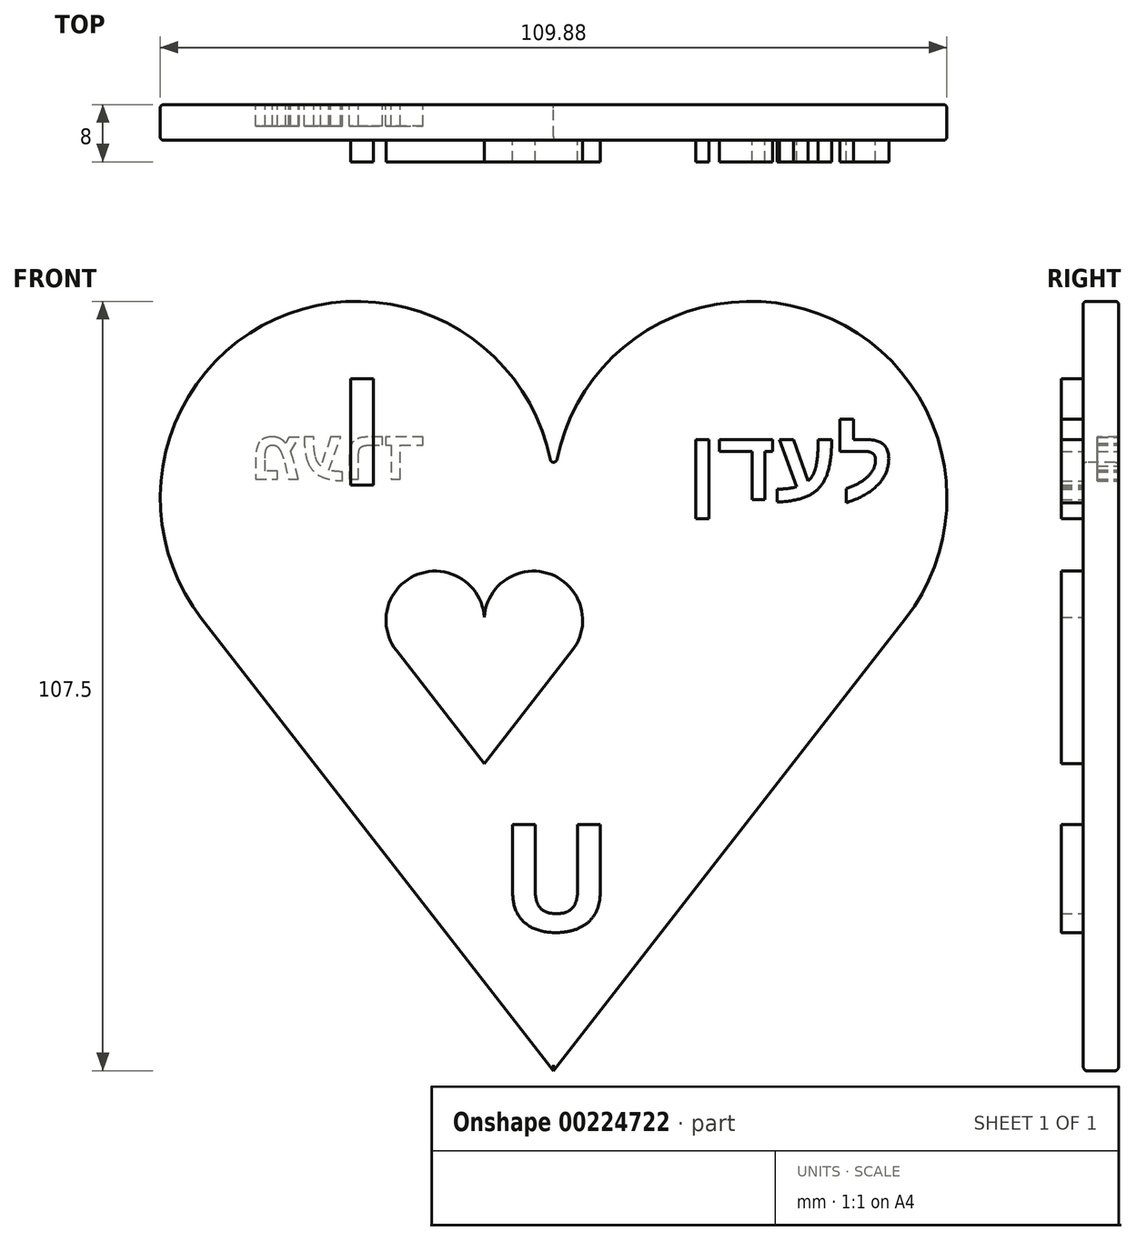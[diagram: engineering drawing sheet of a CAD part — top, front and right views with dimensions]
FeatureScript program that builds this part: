
annotation { "Feature Type Name" : "Feature", "Feature Type Description" : "" }
export const myFeature = defineFeature(function(context is Context, id is Id, definition is map)
    precondition{}
    {
        {
            var Q0;
            Q0=qCreatedBy(makeId("Front.planeOp"),FACE);
            var sketch = newSketch(context, id + "F0", { "sketchPlane" : qUnion([Q0])});
            skArc(sketch, "E0", {"start": v(49.14, 10.3) * mm, "mid": v(37.13, 52.91) * mm, "end": v(0, 28.79) * mm});
            skLineSegment(sketch, "E1", {"start": v(0, 28.79) * mm, "end": v(0, -52.83) * mm});
            skLineSegment(sketch, "E2", {"start": v(0, -52.83) * mm, "end": v(49.14, 10.3) * mm});
            skArc(sketch, "E3.MirrorCS", {"start": v(-49.14, 10.3) * mm, "mid": v(-37.13, 52.91) * mm, "end": v(0, 28.79) * mm});
            skLineSegment(sketch, "E4.MirrorCS", {"start": v(0, -52.83) * mm, "end": v(-49.14, 10.3) * mm});
            skSolve(sketch);
        }
        {
            var Q0;
            Q0=makeQuery(id+"F0.imprint","IMPRINT",FACE,{"disambiguationData":[TD([[makeQuery(id+"F0.imprint","IMPRINT",EDGE,{"derivedFrom":sQuery(id+"F0.wireOp",EDGE,"E1")}),-1.0]])]});
            var Q1;
            Q1=makeQuery(id+"F0.imprint","IMPRINT",FACE,{"disambiguationData":[TD([[makeQuery(id+"F0.imprint","IMPRINT",EDGE,{"derivedFrom":sQuery(id+"F0.wireOp",EDGE,"E0")}),1.0]])]});
            extrude(context, id + "F1", {"entities" : qUnion([Q0, Q1]), "depth" : 5 * mm});
        }
        {
            var Q0;
            Q0=qCreatedBy(makeId("Front.planeOp"),FACE);
            var sketch = newSketch(context, id + "F2", { "sketchPlane" : qUnion([Q0])});
            skArc(sketch, "E5", {"start": v(2.61, 5.88) * mm, "mid": v(-0.4, 16.54) * mm, "end": v(-9.67, 10.5) * mm});
            skLineSegment(sketch, "E6", {"start": v(-9.67, 10.5) * mm, "end": v(-9.67, -9.9) * mm});
            skLineSegment(sketch, "E7", {"start": v(-9.67, -9.9) * mm, "end": v(2.61, 5.88) * mm});
            skArc(sketch, "E8.MirrorCS", {"start": v(-21.96, 5.88) * mm, "mid": v(-18.95, 16.54) * mm, "end": v(-9.67, 10.5) * mm});
            skLineSegment(sketch, "E9.MirrorCS", {"start": v(-9.67, -9.9) * mm, "end": v(-21.96, 5.88) * mm});
            skText(sketch, "E10", { "text": "I", "fontName": "OpenSans-Bold.ttf"});
            skText(sketch, "E11", { "text": "U", "fontName": "OpenSans-Bold.ttf"});
            skText(sketch, "E12", { "text": "ןדעל", "fontName": "Arimo-Bold.ttf"});
            const initialGuessF2  = {"E10": [-0.03022, 0.02897, 1, 0, 0.015], "E11": [-0.00748, -0.03333, 1, 0, 0.015], "E12": [0.01868, 0.02694, 1, 0, 0.01]};
            skSetInitialGuess(sketch, initialGuessF2);
            skSolve(sketch);
        }
        {
            var Q0;
            Q0=makeQuery(id+"F1.opExtrude","CAP_EDGE",EDGE,{"disambiguationData":[OSD([sQuery(id+"F0.wireOp",EDGE,"E3.MirrorCS")])],"isStart":false});
            var Q1;
            Q1=makeQuery(id+"F1.opExtrude","CAP_EDGE",EDGE,{"disambiguationData":[OSD([sQuery(id+"F0.wireOp",EDGE,"E4.MirrorCS")])],"isStart":false});
            var Q2;
            Q2=makeQuery(id+"F1.opExtrude","CAP_EDGE",EDGE,{"disambiguationData":[OSD([sQuery(id+"F0.wireOp",EDGE,"E2")])],"isStart":false});
            var Q3;
            Q3=makeQuery(id+"F1.opExtrude","CAP_EDGE",EDGE,{"disambiguationData":[OSD([sQuery(id+"F0.wireOp",EDGE,"E0")])],"isStart":false});
            var Q4;
            Q4=makeQuery(id+"F1.opExtrude","SWEPT_EDGE",EDGE,{"disambiguationData":[OSD([sQuery(id+"F0.wireOp",EDGE,"E0"),sQuery(id+"F0.wireOp",EDGE,"E1"),sQuery(id+"F0.wireOp",EDGE,"E3.MirrorCS")])]});
            var Q5;
            Q5=makeQuery(id+"F1.opExtrude","CAP_EDGE",EDGE,{"disambiguationData":[OSD([sQuery(id+"F0.wireOp",EDGE,"E3.MirrorCS")])],"isStart":true});
            var Q6;
            Q6=makeQuery(id+"F1.opExtrude","CAP_EDGE",EDGE,{"disambiguationData":[OSD([sQuery(id+"F0.wireOp",EDGE,"E4.MirrorCS")])],"isStart":true});
            var Q7;
            Q7=makeQuery(id+"F1.opExtrude","CAP_EDGE",EDGE,{"disambiguationData":[OSD([sQuery(id+"F0.wireOp",EDGE,"E0")])],"isStart":true});
            var Q8;
            Q8=makeQuery(id+"F1.opExtrude","CAP_EDGE",EDGE,{"disambiguationData":[OSD([sQuery(id+"F0.wireOp",EDGE,"E2")])],"isStart":true});
            fillet(context, id + "F3", {"entities" : qUnion([Q0, Q1, Q2, Q3, Q4, Q5, Q6, Q7, Q8]), "radius" : 0.5 * mm, "tangentPropagation" : true, "allowEdgeOverflow" : false});
        }
        {
            var Q0;
            Q0=makeQuery(id+"F2.imprint","IMPRINT",FACE,{"disambiguationData":[TD([[makeQuery(id+"F2.imprint","IMPRINT",EDGE,{"derivedFrom":sQuery(id+"F2.wireOp",EDGE,"E5")}),1.0]])]});
            var Q1;
            Q1=makeQuery(id+"F2.imprint","IMPRINT",FACE,{"disambiguationData":[TD([[makeQuery(id+"F2.imprint","IMPRINT",EDGE,{"derivedFrom":sQuery(id+"F2.wireOp",EDGE,"E6")}),-1.0]])]});
            var Q2;
            Q2 = qSketchRegion(id + "F2", true);
            var Q3;
            Q3=makeQuery(id+"F2.imprint","IMPRINT",FACE,{"disambiguationData":[TD([[makeQuery(id+"F2.imprint","IMPRINT",EDGE,{"derivedFrom":sQuery(id+"F2.wireOp",EDGE,"E10.sketch_text.stroke-0")}),-1.0]])]});
            var Q4;
            Q4=makeQuery(id+"F2.imprint","IMPRINT",FACE,{"disambiguationData":[TD([[makeQuery(id+"F2.imprint","IMPRINT",EDGE,{"derivedFrom":sQuery(id+"F2.wireOp",EDGE,"E11.sketch_text.stroke-0")}),-1.0]])]});
            var Q5;
            Q5=makeQuery(id+"F2.imprint","IMPRINT",FACE,{"disambiguationData":[TD([[makeQuery(id+"F2.imprint","IMPRINT",EDGE,{"derivedFrom":sQuery(id+"F2.wireOp",EDGE,"E12.sketch_text.stroke-4")}),-1.0]])]});
            var Q6;
            Q6=makeQuery(id+"F2.imprint","IMPRINT",FACE,{"disambiguationData":[TD([[makeQuery(id+"F2.imprint","IMPRINT",EDGE,{"derivedFrom":sQuery(id+"F2.wireOp",EDGE,"E12.sketch_text.stroke-12")}),-1.0]])]});
            var Q7;
            Q7=makeQuery(id+"F2.imprint","IMPRINT",FACE,{"disambiguationData":[TD([[makeQuery(id+"F2.imprint","IMPRINT",EDGE,{"derivedFrom":sQuery(id+"F2.wireOp",EDGE,"E12.sketch_text.stroke-23")}),-1.0]])]});
            var Q8;
            Q8=makeQuery(id+"F2.imprint","IMPRINT",FACE,{"disambiguationData":[TD([[makeQuery(id+"F2.imprint","IMPRINT",EDGE,{"derivedFrom":sQuery(id+"F2.wireOp",EDGE,"E12.sketch_text.stroke-0")}),-1.0]])]});
            var Q9;
            Q9=sQuery(id+"F2.wireOp",EDGE,"E6");
            extrude(context, id + "F4", {"entities" : qUnion([Q0, Q1, Q2, Q3, Q4, Q5, Q6, Q7, Q8]), "operationType" : NewBodyOperationType.ADD, "surfaceEntities" : qUnion([Q9]), "depth" : 8 * mm});
        }
        {
            var Q0;
            Q0=makeQuery(id+"F1.opExtrude","CAP_FACE",FACE,{"disambiguationData":[OSD([sQuery(id+"F0.wireOp",EDGE,"E0"),sQuery(id+"F0.wireOp",EDGE,"E2"),sQuery(id+"F0.wireOp",EDGE,"E3.MirrorCS"),sQuery(id+"F0.wireOp",EDGE,"E4.MirrorCS")])],"isStart":true});
            var sketch = newSketch(context, id + "F5", { "sketchPlane" : qUnion([Q0])});
            skText(sketch, "E13", { "text": "דרעמ", "fontName": "Arimo-Bold.ttf"});
            const initialGuessF5  = {"E13": [0.01804, 0.02982, 1, 0, 0.007]};
            skSetInitialGuess(sketch, initialGuessF5);
            skSolve(sketch);
        }
        {
            var Q0;
            Q0 = qSketchRegion(id + "F5", true);
            extrude(context, id + "F6", {"entities" : qUnion([Q0]), "operationType" : NewBodyOperationType.REMOVE, "oppositeDirection" : true, "depth" : 3 * mm});
        }
    });
